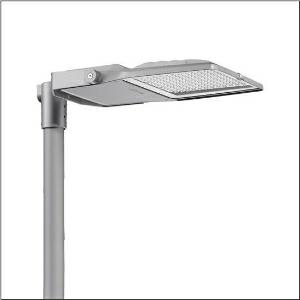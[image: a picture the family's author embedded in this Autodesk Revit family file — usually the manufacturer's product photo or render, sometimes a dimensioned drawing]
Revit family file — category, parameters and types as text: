
# Revit family: floodlight_fl_21_iq_midi___pl43_5xa7782e2a3a_72be
name_source: partatom
category: Lighting Fixtures
units: mm (PartAtom-declared; Revit-internal decimal feet)

## family parameters
Cut with Voids When Loaded = No
Host = Face
Light Source = No
Part Type = Normal
Room Calculation Point = No
Round Connector Dimension = Use Diameter
Shared = No

## types (1)
- --- (1 x LED, 27540 lm, 208.1 W, 3000K)
    Apparent Load = 208 VA
    CIE Flux Codes = 27 78 99 100 100
    Color Rendering = 70
    Color Temperature = 3000K
    Default Elevation = 1800 mm
    Description = Floodlight FL 21 iQ midi, floodlight, primary light control with lens, of PMMA, primary optical cover: protective disc, of toughened safety glass, transparent, light distribution: PL43, light emission: direct distribution, installation type: surface-mounted, LED, High Power LED, rated luminous flux: 27.540lm, luminous efficacy: 132lm/W, light colour: 730, colour temperature: 3000K, control gear: iQ Street-Remote/DALI, control: optimised constant luminous flux control (CLO 2.0), Desk-Remote (wireless, voltage-free reading and setting of iQ features in the workshop via application-optimized NFC function/RFID function), Smart-Wire, Night-Set, Temp-Guard, Auto-Match, Street-Remote, with terminal, 6-pole, mains connection: 220..240V, AC, 50/60Hz, start of lifetime: 208W, end of service life: 227W, reduction: 90W, luminaire housing, of diecast aluminium, powder-coated, Siteco® metallic grey (DB 702S), corrosivity category C5 mid according to DIN EN ISO 12944, suitable for swimming pools, chlorine-resistant, sealing non-destructively replaceable, please order mast flange separately, mast bracket, of steel, galvanised, powder-coated, Siteco® metallic grey (DB 702S), protection rating (complete): IP66, insulation class (complete): insulation class II (safety insulation), certification: CE, ENEC, VDE, protection symbol: D, impact resistance: IK08, permissible operating ambient temperature: -40..+40°C, permissible operating ambient temperature for outdoor applications: -40..+50°C, standard: DIN EN 12944, LABS conformity tested according to VDMA 24364:2018-05, packaging unit: 1 piece

Light Distribution: PL43
    Height = 76 mm
    Lamp = 1 x LED
    Lamp Light Flux = 27540 lm
    Lamp Power = 208.1 W
    Lamp count = 1
    Length = 657 mm
    Luminous efficacy = 132 lm/W
    Manufacturer = Siteco
    ModVariant = No
    Model = 5XA7782E2A3A
    Number of Poles = 1
    OnlyDefault = Yes
    Power Factor = 1
    Product Name = Floodlight FL 21 iQ midi | PL43
    Product group = floodlight | pylon annexe
    ProductGroupID = 6200
    Protection Class = Protection class II
    Protection Degree = IP 66
    RLX_Detail_Level = 1
    RLX_Emergency_Light_Flux = 0 lm
    RLX_Emergency_Type = 0
    RLX_Emergency_Type_DB = No
    RlxData = <blob elided: 153773 chars, md5=22fccda1>
    Socket = socket
    Standby Power = 0 W
    System Light Flux = 27540 lm
    System Power = 208 W
    Type Comments = factory setting: luminous flux: 100 % | dim-lin: 254 | 710 mA
    Type Image = l_1007123.jpg
    URL = http://relux.com
    VarID = @adj_105186
    Voltage = 0 V
    Weight = 0.00 kg
    Width = 442 mm

## geometry (parser evidence)
native form markers: Blend x4, Sweep x14
no freeform markers — native parametric forms only
